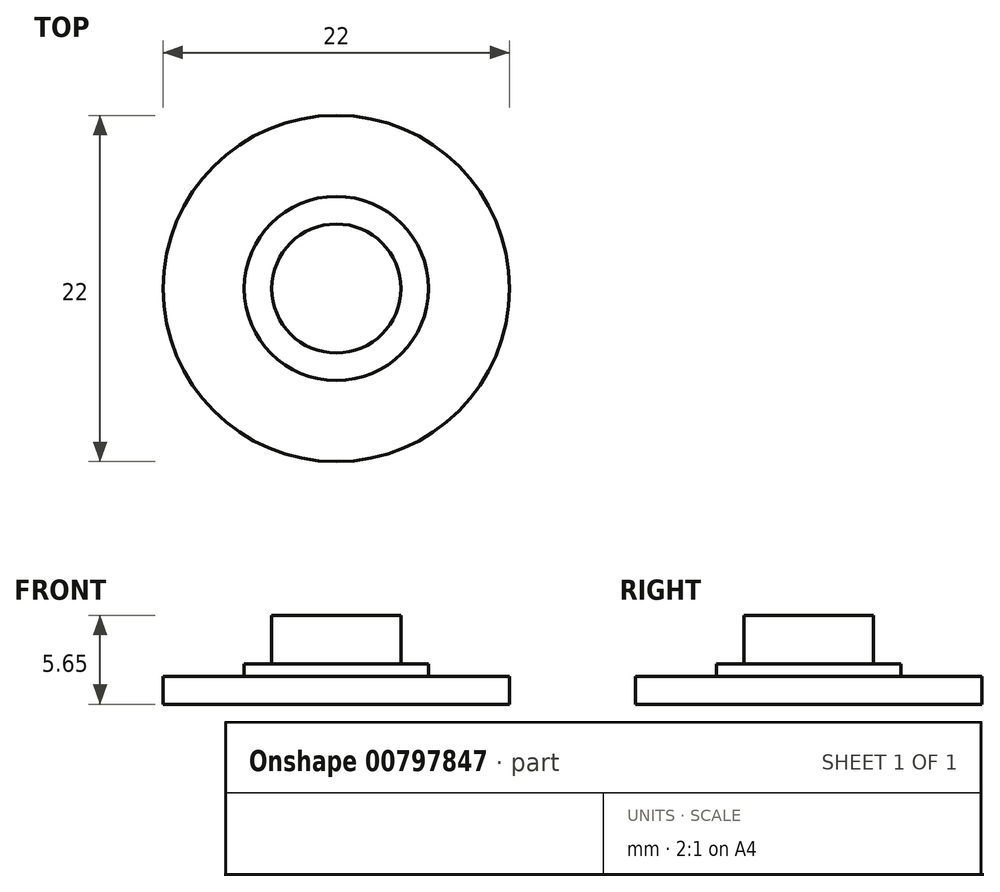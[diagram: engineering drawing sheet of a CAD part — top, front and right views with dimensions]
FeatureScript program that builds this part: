
annotation { "Feature Type Name" : "Feature", "Feature Type Description" : "" }
export const myFeature = defineFeature(function(context is Context, id is Id, definition is map)
    precondition{}
    {
        {
            var Q0;
            Q0=qCreatedBy(makeId("Front.planeOp"),FACE);
            var sketch = newSketch(context, id + "F0", { "sketchPlane" : qUnion([Q0])});
            skLineSegment(sketch, "E0", {"start": v(11, 0) * mm, "end": v(11, 1.75) * mm});
            skLineSegment(sketch, "E1", {"start": v(11, 1.75) * mm, "end": v(5.85, 1.75) * mm});
            skLineSegment(sketch, "E2", {"start": v(5.85, 1.75) * mm, "end": v(5.85, 2.55) * mm});
            skLineSegment(sketch, "E3", {"start": v(5.85, 2.55) * mm, "end": v(4.1, 2.55) * mm});
            skLineSegment(sketch, "E4", {"start": v(4.1, 2.55) * mm, "end": v(4.1, 5.65) * mm});
            skLineSegment(sketch, "E5", {"start": v(4.1, 5.65) * mm, "end": v(0, 5.65) * mm});
            skLineSegment(sketch, "E6", {"start": v(11, 0) * mm, "end": v(0, 0) * mm});
            skLineSegment(sketch, "E7", {"start": v(0, 5.65) * mm, "end": v(0, 0) * mm});
            skSolve(sketch);
        }
        {
            var Q0;
            Q0=makeQuery(id+"F0.imprint","IMPRINT",FACE,{"disambiguationData":[TD([[makeQuery(id+"F0.imprint","IMPRINT",EDGE,{"derivedFrom":sQuery(id+"F0.wireOp",EDGE,"E0")}),1.0]])]});
            var Q1;
            Q1=sQuery(id+"F0.wireOp",EDGE,"E7");
            revolve(context, id + "F1", {"surfaceOperationType" : NewSurfaceOperationType.NEW, "entities" : qUnion([Q0]), "axis" : qUnion([Q1]), "revolveType" : RevolveType.FULL});
        }
    });
